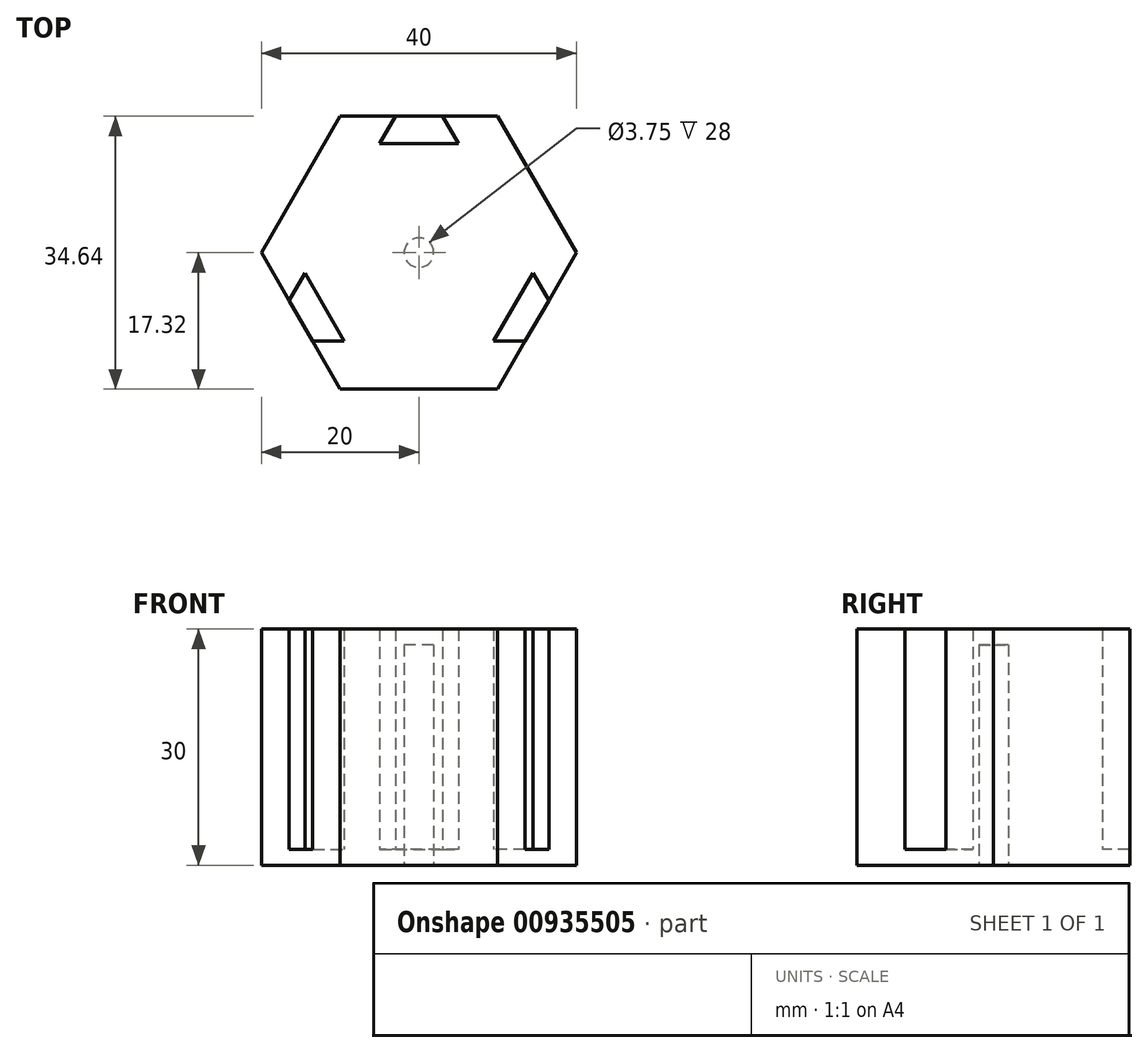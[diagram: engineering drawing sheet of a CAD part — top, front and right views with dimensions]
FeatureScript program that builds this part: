
annotation { "Feature Type Name" : "Feature", "Feature Type Description" : "" }
export const myFeature = defineFeature(function(context is Context, id is Id, definition is map)
    precondition{}
    {
        {
            var Q0;
            Q0=qCreatedBy(makeId("Top.planeOp"),FACE);
            var sketch = newSketch(context, id + "F0", { "sketchPlane" : qUnion([Q0])});
            skCircle(sketch, "E0.cCircle", {"center": v(0, 0) * mm, "radius": 20 * mm, "construction": true});
            skLineSegment(sketch, "E0.0", {"start": v(20, 0) * mm, "end": v(10, -17.32) * mm});
            skLineSegment(sketch, "E0.1", {"start": v(10, -17.32) * mm, "end": v(-10, -17.32) * mm});
            skLineSegment(sketch, "E0.2", {"start": v(-10, -17.32) * mm, "end": v(-20, 0) * mm});
            skLineSegment(sketch, "E0.3", {"start": v(-20, 0) * mm, "end": v(-10, 17.32) * mm});
            skLineSegment(sketch, "E0.4", {"start": v(-10, 17.32) * mm, "end": v(10, 17.32) * mm});
            skLineSegment(sketch, "E0.5", {"start": v(10, 17.32) * mm, "end": v(20, 0) * mm});
            skLineSegment(sketch, "E1", {"start": v(-3, 17.32) * mm, "end": v(3, 17.32) * mm});
            skLineSegment(sketch, "E2", {"start": v(3, 17.32) * mm, "end": v(5, 13.86) * mm});
            skLineSegment(sketch, "E3", {"start": v(5, 13.86) * mm, "end": v(-5, 13.86) * mm});
            skLineSegment(sketch, "E4", {"start": v(-5, 13.86) * mm, "end": v(-3, 17.32) * mm});
            skLineSegment(sketch, "E5.1.0", {"start": v(-16.5, -6.06) * mm, "end": v(-14.5, -2.6) * mm});
            skLineSegment(sketch, "E5.1.1", {"start": v(-14.5, -2.6) * mm, "end": v(-9.5, -11.26) * mm});
            skLineSegment(sketch, "E5.1.2", {"start": v(-9.5, -11.26) * mm, "end": v(-13.5, -11.26) * mm});
            skLineSegment(sketch, "E5.2.0", {"start": v(13.5, -11.26) * mm, "end": v(9.5, -11.26) * mm});
            skLineSegment(sketch, "E5.2.1", {"start": v(9.5, -11.26) * mm, "end": v(14.5, -2.6) * mm});
            skLineSegment(sketch, "E5.2.2", {"start": v(14.5, -2.6) * mm, "end": v(16.5, -6.06) * mm});
            skCircle(sketch, "E6", {"center": v(0, 0) * mm, "radius": 1.88 * mm});
            skSolve(sketch);
        }
        {
            var Q0;
            {var subQ10=sQuery(id+"F0.wireOp",EDGE,"E0.1");Q0=makeQuery(id+"F0.imprint","IMPRINT",FACE,{"disambiguationData":[TD([[makeQuery(id+"F0.imprint","IMPRINT",EDGE,{"derivedFrom":subQ10}),-1.0]])]});}
            extrude(context, id + "F1", {"entities" : qUnion([Q0]), "depth" : 30 * mm, "offsetDistance" : 25 * mm});
        }
        {
            var Q0;
            {var subQ0=sQuery(id+"F0.wireOp",EDGE,"E5.2.0");Q0=makeQuery(id+"F0.imprint","IMPRINT",FACE,{"disambiguationData":[TD([[makeQuery(id+"F0.imprint","IMPRINT",EDGE,{"derivedFrom":subQ0}),-1.0]])]});}
            var Q1;
            {var subQ0=sQuery(id+"F0.wireOp",EDGE,"E5.1.0");Q1=makeQuery(id+"F0.imprint","IMPRINT",FACE,{"disambiguationData":[TD([[makeQuery(id+"F0.imprint","IMPRINT",EDGE,{"derivedFrom":subQ0}),-1.0]])]});}
            var Q2;
            {var subQ0=sQuery(id+"F0.wireOp",EDGE,"E2");Q2=makeQuery(id+"F0.imprint","IMPRINT",FACE,{"disambiguationData":[TD([[makeQuery(id+"F0.imprint","IMPRINT",EDGE,{"derivedFrom":subQ0}),-1.0]])]});}
            extrude(context, id + "F2", {"entities" : qUnion([Q0, Q1, Q2]), "operationType" : NewBodyOperationType.ADD, "depth" : 2 * mm, "offsetDistance" : 25 * mm});
        }
        {
            var Q0;
            Q0=makeQuery(id+"F0.imprint","IMPRINT",FACE,{"disambiguationData":[TD([[makeQuery(id+"F0.imprint","IMPRINT",EDGE,{"derivedFrom":sQuery(id+"F0.wireOp",EDGE,"E6")}),1.0]])]});
            extrude(context, id + "F3", {"entities" : qUnion([Q0]), "operationType" : NewBodyOperationType.ADD, "depth" : 30 * mm, "offsetDistance" : 25 * mm, "hasSecondDirection" : true, "secondDirectionOppositeDirection" : false, "secondDirectionDepth" : 28 * mm});
        }
    });
